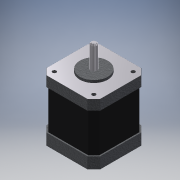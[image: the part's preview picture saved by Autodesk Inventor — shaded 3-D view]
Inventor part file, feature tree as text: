
AUTODESK INVENTOR PART (.ipt)
format: ipt  version: 2016 SP1 (Build 200210100, 210)  size: 503,296 bytes
history: native  units: mm
features: extrude x19, sketch x19, mirror x7, projected_geometry x7, chamfer x4, thread x4, fillet x2, plane x1, pattern_linear x1
ambient origin geometry x8: Origin, YZ Plane, XZ Plane, XY Plane, X Axis, Y Axis, Z Axis, Center Point
bodies: Solid1 (feature_tree)
feature tree (64):
  extrude  "Extrusion1"  Depth=42.3mm
  extrude  "Extrusion2"  Depth=21.15mm
  extrude  "Extrusion3"  Depth=22.0mm
  chamfer  "Chamfer1"  Distance=2.0mm
  plane  "Work Plane1"
  extrude  "Extrusion4"  Depth=18.0mm TaperAngle=0.0deg
  extrude  "Extrusion5"  [1 undecoded]
  fillet  "Fillet1"  Radius=1.0mm
  chamfer  "Chamfer2"  Distance=31.0mm
  thread  "Thread1"  [1 undecoded]
  thread  "Thread2"  [1 undecoded]
  thread  "Thread3"  [1 undecoded]
  thread  "Thread4"  [1 undecoded]
  extrude  "Extrusion7"  Depth=1.0mm TaperAngle=45.0deg
  extrude  "Extrusion8"  Depth=10.0mm TaperAngle=0.0deg
  extrude  "Extrusion9"  Depth=10.0mm TaperAngle=0.0deg
  extrude  "Extrusion10"  Depth=8.15mm
  extrude  "Extrusion11"  Depth=3.0mm TaperAngle=0.0deg
  extrude  "Extrusion12"  Depth=7.0mm TaperAngle=0.0deg
  mirror  "Mirror1"
  extrude  "Extrusion13"  Depth=4.75mm TaperAngle=0.0deg
  mirror  "Mirror2"
  extrude  "Extrusion14"  Depth=4.0mm
  chamfer  "Chamfer3"  Distance=1.0mm
  pattern_linear  "Rectangular Pattern1"  Spacing1=0.75mm  [1 undecoded]
  mirror  "Mirror3"
  extrude  "Extrusion15"  Depth=3.55mm
  extrude  "Extrusion16"  Depth=3.55mm
  mirror  "Mirror4"
  mirror  "Mirror5"
  extrude  "Extrusion17"  Depth=3.55mm
  extrude  "Extrusion18"  Depth=3.55mm TaperAngle=0.0deg
  fillet  "Fillet2"  Radius=0.08mm
  mirror  "Mirror6"
  mirror  "Mirror7"
  extrude  "Extrusion19"  Depth=2.5mm
  chamfer  "Chamfer4"  Distance=9.19mm
  extrude  "Extrusion20"  Depth=3.55mm TaperAngle=0.0deg
  sketch  "Sketch1"  dims[d0=42.3mm d1=42.3mm]
  sketch  "Sketch2"  dims[d2=21.15mm d3=21.15mm]
  sketch  "Sketch3"  dims[d4=48.0mm d5=0.0mm d6=22.0mm d7=2.0mm d8=0.0mm]
  sketch  "Sketch4"  dims[d9=5.0mm d10=18.0mm d11=0.0mm]
  projected_geometry  "Projected Loop1"
  sketch  "Sketch5"  dims[d12=5.0mm d13=2.0mm d14=45.0deg d15=-8.0mm d16=1.0mm d17=31.0mm d18=0.0mm d19=3.0mm d20=15.5mm d21=15.5mm d22=4.0mm d23=0.0mm]
  sketch  "Sketch7"  dims[d24=0.1mm d25=1.0mm d26=2.0mm d27=45.0deg]
  sketch  "Sketch8"  dims[d30=10.0mm d31=0.0mm d32=10.0mm d33=0.0mm]
  sketch  "Sketch9"  dims[d34=10.0mm d35=0.0mm d36=10.0mm d37=0.0mm]
  sketch  "Sketch10"  dims[d38=16.3mm d39=8.15mm]
  projected_geometry  "Projected Loop2"
  sketch  "Sketch11"  dims[d40=4.5mm d41=3.0mm d42=0.0mm]
  projected_geometry  "Projected Loop3"
  sketch  "Sketch12"  dims[d43=1.0mm d44=0.0mm d45=7.0mm d46=0.0mm]
  sketch  "Sketch13"  dims[d47=0.6mm d48=4.75mm d49=0.0mm]
  sketch  "Sketch14"  dims[d50=8.0mm d51=4.0mm]
  projected_geometry  "Projected Loop4"
  sketch  "Sketch15"  dims[d52=4.28mm d53=1.0mm d54=0.0mm]
  sketch  "Sketch16"  dims[d55=0.1mm]
  projected_geometry  "Projected Loop5"
  sketch  "Sketch17"  dims[d56=0.1mm d57=0.0mm]
  projected_geometry  "Projected Loop6"
  sketch  "Sketch18"  dims[d59=0.1mm d60=0.0mm]
  projected_geometry  "Projected Loop7"
  sketch  "Sketch19"  dims[d61=0.1mm]
  sketch  "Sketch20"  dims[d62=0.05mm d63=0.75mm d64=0.5mm d65=0.25mm d66=0.5mm d67=4.6mm d68=0.0mm d69=0.08mm d70=2.0mm d71=12.217305mm d72=30.0mm d74=2.5mm d75=9.19mm d76=3.55mm d77=0.0mm d78=15.0mm d79=15.0mm d80=6.0mm d81=2.0mm d82=0.0mm d83=1.7mm d84=0.0mm d85=1.0mm d86=1.0mm d87=1.5mm d88=1.5mm d89=1.5mm d90=1.5mm d91=0.5mm d92=0.5mm d93=0.6mm d94=0.0mm d95=0.5mm d96=5.0mm d97=0.6mm d98=0.0mm d99=0.2mm d100=2.0mm d101=45.0deg d102=2.0mm d103=17.0mm d104=0.0mm]
note: 6 required parameter values undecoded (feature->parameter linkage not recoverable at this tier; creation-order binding heuristic only, values carry confidence <= 0.55)
